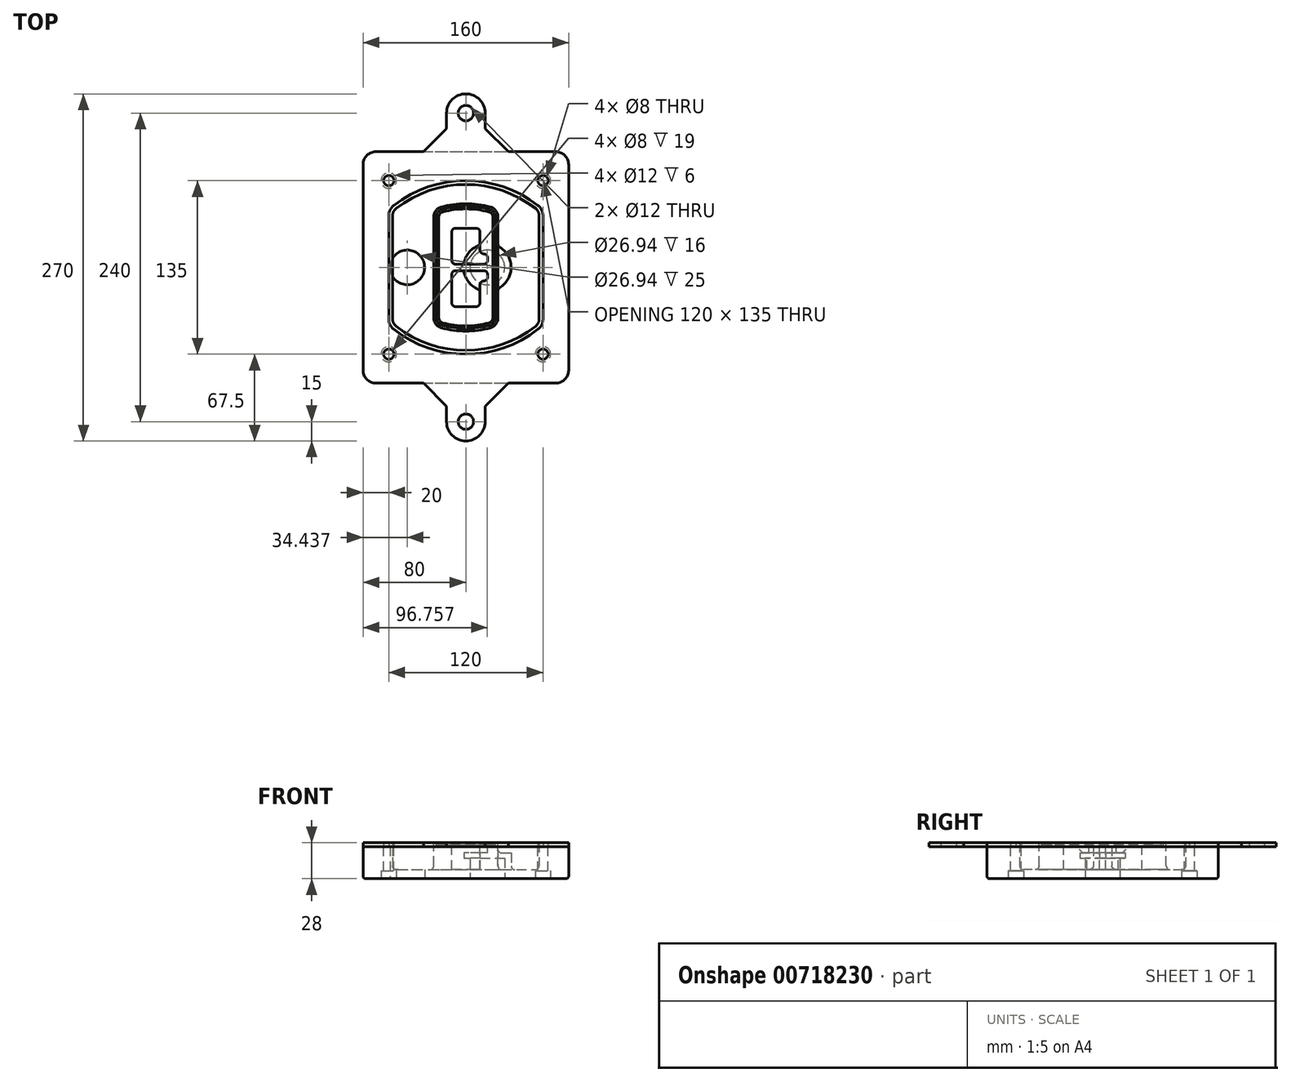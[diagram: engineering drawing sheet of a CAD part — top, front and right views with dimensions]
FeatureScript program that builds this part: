
annotation { "Feature Type Name" : "Feature", "Feature Type Description" : "" }
export const myFeature = defineFeature(function(context is Context, id is Id, definition is map)
    precondition{}
    {
        {
            var Q0;
            Q0=qCreatedBy(makeId("Top.planeOp"),FACE);
            var sketch = newSketch(context, id + "F0", { "sketchPlane" : qUnion([Q0])});
            skPoint(sketch, "E0.rect.middle", {"position": v(0, 0) * mm});
            skLineSegment(sketch, "E1.bottom", {"start": v(-70, -90) * mm, "end": v(70, -90) * mm});
            skLineSegment(sketch, "E1.top", {"start": v(-70, 90) * mm, "end": v(70, 90) * mm});
            skLineSegment(sketch, "E1.left", {"start": v(-80, -80) * mm, "end": v(-80, 80) * mm});
            skLineSegment(sketch, "E1.right", {"start": v(80, -80) * mm, "end": v(80, 80) * mm});
            skLineSegment(sketch, "E2", {"start": v(-80, 90) * mm, "end": v(80, -90) * mm, "construction": true});
            skLineSegment(sketch, "E3", {"start": v(80, 90) * mm, "end": v(-80, -90) * mm, "construction": true});
            skCircle(sketch, "E4", {"center": v(-60, 67.5) * mm, "radius": 4 * mm});
            skCircle(sketch, "E5", {"center": v(60, 67.5) * mm, "radius": 4 * mm});
            skCircle(sketch, "E6", {"center": v(60, -67.5) * mm, "radius": 4 * mm});
            skCircle(sketch, "E7", {"center": v(-60, -67.5) * mm, "radius": 4 * mm});
            skLineSegment(sketch, "E8", {"start": v(-60, 67.5) * mm, "end": v(60, 67.5) * mm, "construction": true});
            skLineSegment(sketch, "E9", {"start": v(60, 67.5) * mm, "end": v(60, -67.5) * mm, "construction": true});
            skLineSegment(sketch, "E10", {"start": v(60, -67.5) * mm, "end": v(-60, -67.5) * mm, "construction": true});
            skLineSegment(sketch, "E11", {"start": v(-60, -67.5) * mm, "end": v(-60, 67.5) * mm, "construction": true});
            skLineSegment(sketch, "E12", {"start": v(-60, 40.3) * mm, "end": v(-60, -40.3) * mm});
            skLineSegment(sketch, "E13", {"start": v(60, 40.3) * mm, "end": v(60, -40.3) * mm});
            skArc(sketch, "E14", {"start": v(56.15, 48.18) * mm, "mid": v(0, 67.5) * mm, "end": v(-56.15, 48.18) * mm});
            skArc(sketch, "E15", {"start": v(-56.15, -48.18) * mm, "mid": v(0, -67.5) * mm, "end": v(56.15, -48.18) * mm});
            skLineSegment(sketch, "E16", {"start": v(-60, 0) * mm, "end": v(60, 0) * mm, "construction": true});
            skPoint(sketch, "E17.visualSharp", {"position": v(-60, -45) * mm});
            skArc(sketch, "E17.filletArc", {"start": v(-60, -40.3) * mm, "mid": v(-58.99, -44.68) * mm, "end": v(-56.15, -48.18) * mm});
            skPoint(sketch, "E18.visualSharp", {"position": v(-60, 45) * mm});
            skArc(sketch, "E18.filletArc", {"start": v(-56.15, 48.18) * mm, "mid": v(-58.99, 44.68) * mm, "end": v(-60, 40.3) * mm});
            skPoint(sketch, "E19.visualSharp", {"position": v(60, 45) * mm});
            skArc(sketch, "E19.filletArc", {"start": v(60, 40.3) * mm, "mid": v(58.99, 44.68) * mm, "end": v(56.15, 48.18) * mm});
            skPoint(sketch, "E20.visualSharp", {"position": v(60, -45) * mm});
            skArc(sketch, "E20.filletArc", {"start": v(56.15, -48.18) * mm, "mid": v(58.99, -44.68) * mm, "end": v(60, -40.3) * mm});
            skPoint(sketch, "E21.visualSharp", {"position": v(-80, 90) * mm});
            skArc(sketch, "E21.filletArc", {"start": v(-70, 90) * mm, "mid": v(-77.07, 87.07) * mm, "end": v(-80, 80) * mm});
            skPoint(sketch, "E22.visualSharp", {"position": v(80, 90) * mm});
            skArc(sketch, "E22.filletArc", {"start": v(80, 80) * mm, "mid": v(77.07, 87.07) * mm, "end": v(70, 90) * mm});
            skPoint(sketch, "E23.visualSharp", {"position": v(80, -90) * mm});
            skArc(sketch, "E23.filletArc", {"start": v(70, -90) * mm, "mid": v(77.07, -87.07) * mm, "end": v(80, -80) * mm});
            skPoint(sketch, "E24.visualSharp", {"position": v(-80, -90) * mm});
            skArc(sketch, "E24.filletArc", {"start": v(-80, -80) * mm, "mid": v(-77.07, -87.07) * mm, "end": v(-70, -90) * mm});
            skArc(sketch, "E25.0", {"start": v(57, 40.3) * mm, "mid": v(56.3, 43.36) * mm, "end": v(54.3, 45.81) * mm});
            skLineSegment(sketch, "E25.1", {"start": v(57, 40.3) * mm, "end": v(57, -40.3) * mm});
            skArc(sketch, "E25.2", {"start": v(54.3, -45.81) * mm, "mid": v(56.3, -43.36) * mm, "end": v(57, -40.3) * mm});
            skArc(sketch, "E25.3", {"start": v(-54.3, -45.81) * mm, "mid": v(0, -64.5) * mm, "end": v(54.3, -45.81) * mm});
            skArc(sketch, "E25.4", {"start": v(-57, -40.3) * mm, "mid": v(-56.3, -43.36) * mm, "end": v(-54.3, -45.81) * mm});
            skArc(sketch, "E25.5", {"start": v(54.3, 45.81) * mm, "mid": v(0, 64.5) * mm, "end": v(-54.3, 45.81) * mm});
            skLineSegment(sketch, "E25.6", {"start": v(-57, 40.3) * mm, "end": v(-57, -40.3) * mm});
            skArc(sketch, "E25.7", {"start": v(-54.3, 45.81) * mm, "mid": v(-56.3, 43.36) * mm, "end": v(-57, 40.3) * mm});
            skArc(sketch, "E26.0", {"start": v(-58.62, 51.33) * mm, "mid": v(-62.58, 46.43) * mm, "end": v(-64, 40.3) * mm});
            skArc(sketch, "E26.1", {"start": v(58.62, 51.33) * mm, "mid": v(0, 71.5) * mm, "end": v(-58.62, 51.33) * mm});
            skArc(sketch, "E26.2", {"start": v(64, 40.3) * mm, "mid": v(62.58, 46.43) * mm, "end": v(58.62, 51.33) * mm});
            skLineSegment(sketch, "E26.3", {"start": v(64, 40.3) * mm, "end": v(64, -40.3) * mm});
            skArc(sketch, "E26.4", {"start": v(58.62, -51.33) * mm, "mid": v(62.58, -46.43) * mm, "end": v(64, -40.3) * mm});
            skLineSegment(sketch, "E26.5", {"start": v(-64, 40.3) * mm, "end": v(-64, -40.3) * mm});
            skArc(sketch, "E26.6", {"start": v(-58.62, -51.33) * mm, "mid": v(0, -71.5) * mm, "end": v(58.62, -51.33) * mm});
            skArc(sketch, "E26.7", {"start": v(-64, -40.3) * mm, "mid": v(-62.58, -46.43) * mm, "end": v(-58.62, -51.33) * mm});
            skSolve(sketch);
        }
        {
            var Q0;
            Q0=makeQuery(id+"F0.imprint","IMPRINT",FACE,{"disambiguationData":[TD([[makeQuery(id+"F0.imprint","IMPRINT",EDGE,{"derivedFrom":sQuery(id+"F0.wireOp",EDGE,"E1.bottom")}),1.0]])]});
            var Q1;
            Q1=makeQuery(id+"F0.imprint","IMPRINT",FACE,{"disambiguationData":[TD([[makeQuery(id+"F0.imprint","IMPRINT",EDGE,{"derivedFrom":sQuery(id+"F0.wireOp",EDGE,"E12")}),1.0]])]});
            var Q2;
            Q2=makeQuery(id+"F0.imprint","IMPRINT",FACE,{"disambiguationData":[TD([[makeQuery(id+"F0.imprint","IMPRINT",EDGE,{"derivedFrom":sQuery(id+"F0.wireOp",EDGE,"E25.0")}),1.0]])]});
            var Q3;
            Q3=makeQuery(id+"F0.imprint","IMPRINT",FACE,{"disambiguationData":[TD([[makeQuery(id+"F0.imprint","IMPRINT",EDGE,{"derivedFrom":sQuery(id+"F0.wireOp",EDGE,"E12")}),-1.0]])]});
            extrude(context, id + "F1", {"entities" : qUnion([Q0, Q1, Q2, Q3]), "oppositeDirection" : true, "depth" : 25 * mm});
        }
        {
            var Q0;
            Q0=makeQuery(id+"F0.imprint","IMPRINT",FACE,{"disambiguationData":[TD([[makeQuery(id+"F0.imprint","IMPRINT",EDGE,{"derivedFrom":sQuery(id+"F0.wireOp",EDGE,"E12")}),1.0]])]});
            extrude(context, id + "F2", {"entities" : qUnion([Q0]), "operationType" : NewBodyOperationType.ADD, "depth" : 3 * mm});
        }
        {
            var Q0;
            Q0=makeQuery(id+"F0.imprint","IMPRINT",FACE,{"disambiguationData":[TD([[makeQuery(id+"F0.imprint","IMPRINT",EDGE,{"derivedFrom":sQuery(id+"F0.wireOp",EDGE,"E25.0")}),1.0]])]});
            extrude(context, id + "F3", {"entities" : qUnion([Q0]), "operationType" : NewBodyOperationType.REMOVE, "oppositeDirection" : true, "depth" : 18 * mm});
        }
        {
            var Q0;
            Q0=makeQuery(id+"F2.opExtrude","CAP_FACE",FACE,{"disambiguationData":[OSD([sQuery(id+"F0.wireOp",EDGE,"E12"),sQuery(id+"F0.wireOp",EDGE,"E13"),sQuery(id+"F0.wireOp",EDGE,"E14"),sQuery(id+"F0.wireOp",EDGE,"E15"),sQuery(id+"F0.wireOp",EDGE,"E17.filletArc"),sQuery(id+"F0.wireOp",EDGE,"E18.filletArc"),sQuery(id+"F0.wireOp",EDGE,"E19.filletArc"),sQuery(id+"F0.wireOp",EDGE,"E20.filletArc"),sQuery(id+"F0.wireOp",EDGE,"E25.0"),sQuery(id+"F0.wireOp",EDGE,"E25.1"),sQuery(id+"F0.wireOp",EDGE,"E25.2"),sQuery(id+"F0.wireOp",EDGE,"E25.3"),sQuery(id+"F0.wireOp",EDGE,"E25.4"),sQuery(id+"F0.wireOp",EDGE,"E25.5"),sQuery(id+"F0.wireOp",EDGE,"E25.6"),sQuery(id+"F0.wireOp",EDGE,"E25.7")])],"isStart":false});
            var sketch = newSketch(context, id + "F4", { "sketchPlane" : qUnion([Q0])});
            skArc(sketch, "E27.0", {"start": v(-19.08, -46.97) * mm, "mid": v(0, -49.5) * mm, "end": v(19.08, -46.97) * mm});
            skArc(sketch, "E28.0", {"start": v(19.08, 46.97) * mm, "mid": v(0, 49.5) * mm, "end": v(-19.08, 46.97) * mm});
            skLineSegment(sketch, "E29", {"start": v(-25, 39.25) * mm, "end": v(-25, -39.25) * mm});
            skLineSegment(sketch, "E30", {"start": v(25, 39.25) * mm, "end": v(25, -39.25) * mm});
            skLineSegment(sketch, "E31", {"start": v(-25, 45.1) * mm, "end": v(25, 45.1) * mm, "construction": true});
            skLineSegment(sketch, "E32", {"start": v(-25, -45.1) * mm, "end": v(25, -45.1) * mm, "construction": true});
            skPoint(sketch, "E33.visualSharp", {"position": v(-25, 45.1) * mm});
            skArc(sketch, "E33.filletArc", {"start": v(-19.08, 46.97) * mm, "mid": v(-23.35, 44.11) * mm, "end": v(-25, 39.25) * mm});
            skPoint(sketch, "E34.visualSharp", {"position": v(25, 45.1) * mm});
            skArc(sketch, "E34.filletArc", {"start": v(25, 39.25) * mm, "mid": v(23.35, 44.11) * mm, "end": v(19.08, 46.97) * mm});
            skPoint(sketch, "E35.visualSharp", {"position": v(25, -45.1) * mm});
            skArc(sketch, "E35.filletArc", {"start": v(19.08, -46.97) * mm, "mid": v(23.35, -44.11) * mm, "end": v(25, -39.25) * mm});
            skPoint(sketch, "E36.visualSharp", {"position": v(-25, -45.1) * mm});
            skArc(sketch, "E36.filletArc", {"start": v(-25, -39.25) * mm, "mid": v(-23.35, -44.11) * mm, "end": v(-19.08, -46.97) * mm});
            skArc(sketch, "E37.0", {"start": v(54.3, 45.81) * mm, "mid": v(0, 64.5) * mm, "end": v(-54.3, 45.81) * mm});
            skArc(sketch, "E37.1", {"start": v(-54.3, 45.81) * mm, "mid": v(-56.3, 43.36) * mm, "end": v(-57, 40.3) * mm});
            skLineSegment(sketch, "E37.2", {"start": v(-57, 40.3) * mm, "end": v(-57, -40.3) * mm});
            skArc(sketch, "E37.3", {"start": v(-57, -40.3) * mm, "mid": v(-56.3, -43.36) * mm, "end": v(-54.3, -45.81) * mm});
            skArc(sketch, "E37.4", {"start": v(-54.3, -45.81) * mm, "mid": v(0, -64.5) * mm, "end": v(54.3, -45.81) * mm});
            skArc(sketch, "E37.5", {"start": v(54.3, -45.81) * mm, "mid": v(56.3, -43.36) * mm, "end": v(57, -40.3) * mm});
            skLineSegment(sketch, "E37.6", {"start": v(57, 40.3) * mm, "end": v(57, -40.3) * mm});
            skArc(sketch, "E37.7", {"start": v(57, 40.3) * mm, "mid": v(56.3, 43.36) * mm, "end": v(54.3, 45.81) * mm});
            skLineSegment(sketch, "E38.0", {"start": v(23, 39.25) * mm, "end": v(23, -39.25) * mm});
            skArc(sketch, "E38.1", {"start": v(18.56, -45.04) * mm, "mid": v(21.76, -42.9) * mm, "end": v(23, -39.25) * mm});
            skArc(sketch, "E38.2", {"start": v(-18.56, -45.04) * mm, "mid": v(0, -47.5) * mm, "end": v(18.56, -45.04) * mm});
            skArc(sketch, "E38.3", {"start": v(-23, -39.25) * mm, "mid": v(-21.76, -42.9) * mm, "end": v(-18.56, -45.04) * mm});
            skLineSegment(sketch, "E38.4", {"start": v(-23, 39.25) * mm, "end": v(-23, -39.25) * mm});
            skArc(sketch, "E38.5", {"start": v(23, 39.25) * mm, "mid": v(21.76, 42.9) * mm, "end": v(18.56, 45.04) * mm});
            skArc(sketch, "E38.6", {"start": v(-18.56, 45.04) * mm, "mid": v(-21.76, 42.9) * mm, "end": v(-23, 39.25) * mm});
            skArc(sketch, "E38.7", {"start": v(18.56, 45.04) * mm, "mid": v(0, 47.5) * mm, "end": v(-18.56, 45.04) * mm});
            skArc(sketch, "E39.0", {"start": v(21, 39.25) * mm, "mid": v(20.18, 41.68) * mm, "end": v(18.04, 43.1) * mm});
            skLineSegment(sketch, "E39.1", {"start": v(21, 39.25) * mm, "end": v(21, -39.25) * mm});
            skArc(sketch, "E39.2", {"start": v(18.04, -43.1) * mm, "mid": v(20.18, -41.68) * mm, "end": v(21, -39.25) * mm});
            skArc(sketch, "E39.3", {"start": v(-18.04, -43.1) * mm, "mid": v(0, -45.5) * mm, "end": v(18.04, -43.1) * mm});
            skArc(sketch, "E39.4", {"start": v(-21, -39.25) * mm, "mid": v(-20.18, -41.68) * mm, "end": v(-18.04, -43.1) * mm});
            skArc(sketch, "E39.5", {"start": v(18.04, 43.1) * mm, "mid": v(0, 45.5) * mm, "end": v(-18.04, 43.1) * mm});
            skLineSegment(sketch, "E39.6", {"start": v(-21, 39.25) * mm, "end": v(-21, -39.25) * mm});
            skArc(sketch, "E39.7", {"start": v(-18.04, 43.1) * mm, "mid": v(-20.18, 41.68) * mm, "end": v(-21, 39.25) * mm});
            skLineSegment(sketch, "E40", {"start": v(-25, 0) * mm, "end": v(25, 0) * mm, "construction": true});
            skLineSegment(sketch, "E41", {"start": v(-11, 5.5) * mm, "end": v(-11, 27.5) * mm});
            skLineSegment(sketch, "E42", {"start": v(-8, 30.5) * mm, "end": v(8, 30.5) * mm});
            skLineSegment(sketch, "E43", {"start": v(11, 27.5) * mm, "end": v(11, 13.5) * mm});
            skLineSegment(sketch, "E44", {"start": v(14, 10.5) * mm, "end": v(14, 10.5) * mm});
            skLineSegment(sketch, "E45", {"start": v(17, 7.5) * mm, "end": v(17, 5.5) * mm});
            skLineSegment(sketch, "E46", {"start": v(14, 2.5) * mm, "end": v(-8, 2.5) * mm});
            skPoint(sketch, "E47.visualSharp", {"position": v(-11, 30.5) * mm});
            skArc(sketch, "E47.filletArc", {"start": v(-8, 30.5) * mm, "mid": v(-10.12, 29.62) * mm, "end": v(-11, 27.5) * mm});
            skPoint(sketch, "E48.visualSharp", {"position": v(11, 30.5) * mm});
            skArc(sketch, "E48.filletArc", {"start": v(11, 27.5) * mm, "mid": v(10.12, 29.62) * mm, "end": v(8, 30.5) * mm});
            skPoint(sketch, "E49.visualSharp", {"position": v(11, 10.5) * mm});
            skArc(sketch, "E49.filletArc", {"start": v(11, 13.5) * mm, "mid": v(11.88, 11.38) * mm, "end": v(14, 10.5) * mm});
            skPoint(sketch, "E50.visualSharp", {"position": v(17, 10.5) * mm});
            skArc(sketch, "E50.filletArc", {"start": v(17, 7.5) * mm, "mid": v(16.12, 9.62) * mm, "end": v(14, 10.5) * mm});
            skPoint(sketch, "E51.visualSharp", {"position": v(17, 2.5) * mm});
            skArc(sketch, "E51.filletArc", {"start": v(14, 2.5) * mm, "mid": v(16.12, 3.38) * mm, "end": v(17, 5.5) * mm});
            skPoint(sketch, "E52.visualSharp", {"position": v(-11, 2.5) * mm});
            skArc(sketch, "E52.filletArc", {"start": v(-11, 5.5) * mm, "mid": v(-10.12, 3.38) * mm, "end": v(-8, 2.5) * mm});
            skLineSegment(sketch, "E53.0.MirrorCS", {"start": v(14, -2.5) * mm, "end": v(-8, -2.5) * mm});
            skArc(sketch, "E54.0.MirrorCS", {"start": v(-11, -5.5) * mm, "mid": v(-10.12, -3.38) * mm, "end": v(-8, -2.5) * mm});
            skLineSegment(sketch, "E55.0.MirrorCS", {"start": v(-11, -5.5) * mm, "end": v(-11, -27.5) * mm});
            skArc(sketch, "E56.0.MirrorCS", {"start": v(-8, -30.5) * mm, "mid": v(-10.12, -29.62) * mm, "end": v(-11, -27.5) * mm});
            skLineSegment(sketch, "E57.0.MirrorCS", {"start": v(-8, -30.5) * mm, "end": v(8, -30.5) * mm});
            skArc(sketch, "E58.0.MirrorCS", {"start": v(11, -27.5) * mm, "mid": v(10.12, -29.62) * mm, "end": v(8, -30.5) * mm});
            skLineSegment(sketch, "E59.0.MirrorCS", {"start": v(11, -27.5) * mm, "end": v(11, -13.5) * mm});
            skArc(sketch, "E60.0.MirrorCS", {"start": v(11, -13.5) * mm, "mid": v(11.88, -11.38) * mm, "end": v(14, -10.5) * mm});
            skArc(sketch, "E61.0.MirrorCS", {"start": v(17, -7.5) * mm, "mid": v(16.12, -9.62) * mm, "end": v(14, -10.5) * mm});
            skLineSegment(sketch, "E62.0.MirrorCS", {"start": v(17, -7.5) * mm, "end": v(17, -5.5) * mm});
            skArc(sketch, "E63.0.MirrorCS", {"start": v(14, -2.5) * mm, "mid": v(16.12, -3.38) * mm, "end": v(17, -5.5) * mm});
            skSolve(sketch);
        }
        {
            var Q0;
            Q0=makeQuery(id+"F4.imprint","IMPRINT",FACE,{"disambiguationData":[TD([[makeQuery(id+"F4.imprint","IMPRINT",EDGE,{"derivedFrom":sQuery(id+"F4.wireOp",EDGE,"E27.0")}),1.0]])]});
            var Q1;
            Q1=makeQuery(id+"F4.imprint","IMPRINT",FACE,{"disambiguationData":[TD([[makeQuery(id+"F4.imprint","IMPRINT",EDGE,{"derivedFrom":sQuery(id+"F4.wireOp",EDGE,"E38.0")}),-1.0]])]});
            var Q2;
            Q2=makeQuery(id+"F4.imprint","IMPRINT",FACE,{"disambiguationData":[TD([[makeQuery(id+"F4.imprint","IMPRINT",EDGE,{"derivedFrom":sQuery(id+"F4.wireOp",EDGE,"E39.0")}),1.0]])]});
            extrude(context, id + "F5", {"entities" : qUnion([Q0, Q1, Q2]), "operationType" : NewBodyOperationType.ADD, "endBound" : BoundingType.UP_TO_NEXT, "oppositeDirection" : true, "depth" : 25 * mm});
        }
        {
            var Q0;
            Q0=makeQuery(id+"F4.imprint","IMPRINT",FACE,{"disambiguationData":[TD([[makeQuery(id+"F4.imprint","IMPRINT",EDGE,{"derivedFrom":sQuery(id+"F4.wireOp",EDGE,"E38.0")}),-1.0]])]});
            extrude(context, id + "F6", {"entities" : qUnion([Q0]), "operationType" : NewBodyOperationType.REMOVE, "oppositeDirection" : true, "depth" : 2 * mm});
        }
        {
            var Q0;
            Q0=makeQuery(id+"F1.opExtrude","CAP_FACE",FACE,{"disambiguationData":[OSD([sQuery(id+"F0.wireOp",EDGE,"E1.bottom"),sQuery(id+"F0.wireOp",EDGE,"E1.top"),sQuery(id+"F0.wireOp",EDGE,"E1.left"),sQuery(id+"F0.wireOp",EDGE,"E1.right"),sQuery(id+"F0.wireOp",EDGE,"E4"),sQuery(id+"F0.wireOp",EDGE,"E5"),sQuery(id+"F0.wireOp",EDGE,"E6"),sQuery(id+"F0.wireOp",EDGE,"E7"),sQuery(id+"F0.wireOp",EDGE,"E21.filletArc"),sQuery(id+"F0.wireOp",EDGE,"E22.filletArc"),sQuery(id+"F0.wireOp",EDGE,"E23.filletArc"),sQuery(id+"F0.wireOp",EDGE,"E24.filletArc")])],"isStart":false});
            var sketch = newSketch(context, id + "F7", { "sketchPlane" : qUnion([Q0])});
            skCircle(sketch, "E64", {"center": v(16.76, 0) * mm, "radius": 13.47 * mm});
            skCircle(sketch, "E65", {"center": v(-45.56, 0) * mm, "radius": 13.47 * mm});
            skLineSegment(sketch, "E66", {"start": v(80, 0) * mm, "end": v(-80, 0) * mm});
            skCircle(sketch, "E67", {"center": v(16.76, 0) * mm, "radius": 18.47 * mm});
            skCircle(sketch, "E68", {"center": v(60, -67.5) * mm, "radius": 6 * mm});
            skCircle(sketch, "E69", {"center": v(-60, -67.5) * mm, "radius": 6 * mm});
            skCircle(sketch, "E70", {"center": v(-60, 67.5) * mm, "radius": 6 * mm});
            skCircle(sketch, "E71", {"center": v(60, 67.5) * mm, "radius": 6 * mm});
            skSolve(sketch);
        }
        {
            var Q0;
            {var subQ1=sQuery(id+"F7.wireOp",EDGE,"E66");var subQ4=sQuery(id+"F7.wireOp",EDGE,"E64");var subQ6=makeQuery(id+"F7.imprint","INTERSECT",VERTEX,{"disambiguationData":[OD(0.0)],"derivedFrom":[subQ4,subQ1]});Q0=makeQuery(id+"F7.imprint","IMPRINT",FACE,{"disambiguationData":[TD([[makeQuery(id+"F7.imprint","IMPRINT",EDGE,{"disambiguationData":[TD([[subQ6,-1.0]])],"derivedFrom":subQ4}),-1.0]])]});}
            var Q1;
            {var subQ0=sQuery(id+"F7.wireOp",EDGE,"E66");var subQ1=sQuery(id+"F7.wireOp",EDGE,"E64");var subQ3=makeQuery(id+"F7.imprint","INTERSECT",VERTEX,{"disambiguationData":[OD(0.0)],"derivedFrom":[subQ1,subQ0]});Q1=makeQuery(id+"F7.imprint","IMPRINT",FACE,{"disambiguationData":[TD([[makeQuery(id+"F7.imprint","IMPRINT",EDGE,{"disambiguationData":[TD([[subQ3,-1.0]])],"derivedFrom":subQ1}),1.0]])]});}
            var Q2;
            {var subQ0=sQuery(id+"F7.wireOp",EDGE,"E66");var subQ1=sQuery(id+"F7.wireOp",EDGE,"E64");var subQ3=makeQuery(id+"F7.imprint","INTERSECT",VERTEX,{"disambiguationData":[OD(0.0)],"derivedFrom":[subQ1,subQ0]});Q2=makeQuery(id+"F7.imprint","IMPRINT",FACE,{"disambiguationData":[TD([[makeQuery(id+"F7.imprint","IMPRINT",EDGE,{"disambiguationData":[TD([[subQ3,1.0]])],"derivedFrom":subQ1}),1.0]])]});}
            var Q3;
            {var subQ1=sQuery(id+"F7.wireOp",EDGE,"E66");var subQ4=sQuery(id+"F7.wireOp",EDGE,"E64");var subQ6=makeQuery(id+"F7.imprint","INTERSECT",VERTEX,{"disambiguationData":[OD(0.0)],"derivedFrom":[subQ4,subQ1]});Q3=makeQuery(id+"F7.imprint","IMPRINT",FACE,{"disambiguationData":[TD([[makeQuery(id+"F7.imprint","IMPRINT",EDGE,{"disambiguationData":[TD([[subQ6,1.0]])],"derivedFrom":subQ4}),-1.0]])]});}
            extrude(context, id + "F8", {"entities" : qUnion([Q0, Q1, Q2, Q3]), "operationType" : NewBodyOperationType.ADD, "oppositeDirection" : true, "depth" : 20 * mm});
        }
        {
            var Q0;
            {var subQ0=sQuery(id+"F7.wireOp",EDGE,"E66");var subQ1=sQuery(id+"F7.wireOp",EDGE,"E64");var subQ3=makeQuery(id+"F7.imprint","INTERSECT",VERTEX,{"disambiguationData":[OD(0.0)],"derivedFrom":[subQ1,subQ0]});Q0=makeQuery(id+"F7.imprint","IMPRINT",FACE,{"disambiguationData":[TD([[makeQuery(id+"F7.imprint","IMPRINT",EDGE,{"disambiguationData":[TD([[subQ3,-1.0]])],"derivedFrom":subQ1}),1.0]])]});}
            var Q1;
            {var subQ0=sQuery(id+"F7.wireOp",EDGE,"E66");var subQ1=sQuery(id+"F7.wireOp",EDGE,"E64");var subQ3=makeQuery(id+"F7.imprint","INTERSECT",VERTEX,{"disambiguationData":[OD(0.0)],"derivedFrom":[subQ1,subQ0]});Q1=makeQuery(id+"F7.imprint","IMPRINT",FACE,{"disambiguationData":[TD([[makeQuery(id+"F7.imprint","IMPRINT",EDGE,{"disambiguationData":[TD([[subQ3,1.0]])],"derivedFrom":subQ1}),1.0]])]});}
            extrude(context, id + "F9", {"entities" : qUnion([Q0, Q1]), "operationType" : NewBodyOperationType.REMOVE, "oppositeDirection" : true, "depth" : 16 * mm});
        }
        {
            var Q0;
            {var subQ0=sQuery(id+"F7.wireOp",EDGE,"E66");var subQ1=sQuery(id+"F7.wireOp",EDGE,"E65");var subQ3=makeQuery(id+"F7.imprint","INTERSECT",VERTEX,{"disambiguationData":[OD(0.0)],"derivedFrom":[subQ1,subQ0]});Q0=makeQuery(id+"F7.imprint","IMPRINT",FACE,{"disambiguationData":[TD([[makeQuery(id+"F7.imprint","IMPRINT",EDGE,{"disambiguationData":[TD([[subQ3,-1.0]])],"derivedFrom":subQ1}),1.0]])]});}
            var Q1;
            {var subQ0=sQuery(id+"F7.wireOp",EDGE,"E66");var subQ1=sQuery(id+"F7.wireOp",EDGE,"E65");var subQ3=makeQuery(id+"F7.imprint","INTERSECT",VERTEX,{"disambiguationData":[OD(0.0)],"derivedFrom":[subQ1,subQ0]});Q1=makeQuery(id+"F7.imprint","IMPRINT",FACE,{"disambiguationData":[TD([[makeQuery(id+"F7.imprint","IMPRINT",EDGE,{"disambiguationData":[TD([[subQ3,1.0]])],"derivedFrom":subQ1}),1.0]])]});}
            extrude(context, id + "F10", {"entities" : qUnion([Q0, Q1]), "operationType" : NewBodyOperationType.REMOVE, "oppositeDirection" : true, "depth" : 25 * mm});
        }
        {
            var Q0;
            Q0=makeQuery(id+"F7.imprint","IMPRINT",FACE,{"disambiguationData":[TD([[makeQuery(id+"F7.imprint","IMPRINT",EDGE,{"derivedFrom":sQuery(id+"F7.wireOp",EDGE,"E68")}),1.0]])]});
            var Q1;
            Q1=makeQuery(id+"F7.imprint","IMPRINT",FACE,{"disambiguationData":[TD([[makeQuery(id+"F7.imprint","IMPRINT",EDGE,{"derivedFrom":makeQuery(id+"F1.opExtrude","CAP_EDGE",EDGE,{"disambiguationData":[OSD([sQuery(id+"F0.wireOp",EDGE,"E5")])],"isStart":false})}),-1.0]])]});
            var Q2;
            Q2=makeQuery(id+"F7.imprint","IMPRINT",FACE,{"disambiguationData":[TD([[makeQuery(id+"F7.imprint","IMPRINT",EDGE,{"derivedFrom":sQuery(id+"F7.wireOp",EDGE,"E69")}),1.0]])]});
            var Q3;
            Q3=makeQuery(id+"F7.imprint","IMPRINT",FACE,{"disambiguationData":[TD([[makeQuery(id+"F7.imprint","IMPRINT",EDGE,{"derivedFrom":makeQuery(id+"F1.opExtrude","CAP_EDGE",EDGE,{"disambiguationData":[OSD([sQuery(id+"F0.wireOp",EDGE,"E4")])],"isStart":false})}),-1.0]])]});
            var Q4;
            Q4=makeQuery(id+"F7.imprint","IMPRINT",FACE,{"disambiguationData":[TD([[makeQuery(id+"F7.imprint","IMPRINT",EDGE,{"derivedFrom":sQuery(id+"F7.wireOp",EDGE,"E70")}),1.0]])]});
            var Q5;
            Q5=makeQuery(id+"F7.imprint","IMPRINT",FACE,{"disambiguationData":[TD([[makeQuery(id+"F7.imprint","IMPRINT",EDGE,{"derivedFrom":makeQuery(id+"F1.opExtrude","CAP_EDGE",EDGE,{"disambiguationData":[OSD([sQuery(id+"F0.wireOp",EDGE,"E7")])],"isStart":false})}),-1.0]])]});
            var Q6;
            Q6=makeQuery(id+"F7.imprint","IMPRINT",FACE,{"disambiguationData":[TD([[makeQuery(id+"F7.imprint","IMPRINT",EDGE,{"derivedFrom":sQuery(id+"F7.wireOp",EDGE,"E71")}),1.0]])]});
            var Q7;
            Q7=makeQuery(id+"F7.imprint","IMPRINT",FACE,{"disambiguationData":[TD([[makeQuery(id+"F7.imprint","IMPRINT",EDGE,{"derivedFrom":makeQuery(id+"F1.opExtrude","CAP_EDGE",EDGE,{"disambiguationData":[OSD([sQuery(id+"F0.wireOp",EDGE,"E6")])],"isStart":false})}),-1.0]])]});
            extrude(context, id + "F11", {"entities" : qUnion([Q0, Q1, Q2, Q3, Q4, Q5, Q6, Q7]), "operationType" : NewBodyOperationType.REMOVE, "oppositeDirection" : true, "depth" : 6 * mm});
        }
        {
            var Q0;
            Q0=makeQuery(id+"F9.boolean.opBoolean","COPY",FACE,{"derivedFrom":makeQuery(id+"F9.opExtrude","CAP_FACE",FACE,{"disambiguationData":[OSD([sQuery(id+"F7.wireOp",EDGE,"E64")])],"isStart":false})});
            var sketch = newSketch(context, id + "F12", { "sketchPlane" : qUnion([Q0])});
            skArc(sketch, "E72.0", {"start": v(11, 17.55) * mm, "mid": v(2.57, 11.82) * mm, "end": v(-1.54, 2.5) * mm});
            skArc(sketch, "E72.1", {"start": v(-1.54, -2.5) * mm, "mid": v(2.57, -11.82) * mm, "end": v(11, -17.55) * mm});
            skLineSegment(sketch, "E73", {"start": v(-1.54, -2.5) * mm, "end": v(14, -2.5) * mm});
            skLineSegment(sketch, "E74.0", {"start": v(14, 2.5) * mm, "end": v(-1.54, 2.5) * mm});
            skArc(sketch, "E74.1", {"start": v(14, 2.5) * mm, "mid": v(16.12, 3.38) * mm, "end": v(17, 5.5) * mm});
            skLineSegment(sketch, "E74.2", {"start": v(17, 7.5) * mm, "end": v(17, 5.5) * mm});
            skArc(sketch, "E74.3", {"start": v(17, 7.5) * mm, "mid": v(16.12, 9.62) * mm, "end": v(14, 10.5) * mm});
            skArc(sketch, "E74.4", {"start": v(11, 13.5) * mm, "mid": v(11.88, 11.38) * mm, "end": v(14, 10.5) * mm});
            skLineSegment(sketch, "E74.5", {"start": v(11, 17.55) * mm, "end": v(11, 13.5) * mm});
            skLineSegment(sketch, "E74.7", {"start": v(14, -2.5) * mm, "end": v(-1.54, -2.5) * mm});
            skArc(sketch, "E74.8", {"start": v(14, -2.5) * mm, "mid": v(16.12, -3.38) * mm, "end": v(17, -5.5) * mm});
            skLineSegment(sketch, "E74.9", {"start": v(17, -7.5) * mm, "end": v(17, -5.5) * mm});
            skArc(sketch, "E74.10", {"start": v(17, -7.5) * mm, "mid": v(16.12, -9.62) * mm, "end": v(14, -10.5) * mm});
            skArc(sketch, "E74.11", {"start": v(11, -13.5) * mm, "mid": v(11.88, -11.38) * mm, "end": v(14, -10.5) * mm});
            skLineSegment(sketch, "E74.12", {"start": v(11, -17.55) * mm, "end": v(11, -13.5) * mm});
            skPoint(sketch, "E75.orphan", {"position": v(11, -27.5) * mm});
            skPoint(sketch, "E76.orphan", {"position": v(-8, -2.5) * mm});
            skPoint(sketch, "E77.orphan", {"position": v(-8, 2.5) * mm});
            skPoint(sketch, "E78.orphan", {"position": v(11, 27.5) * mm});
            skSolve(sketch);
        }
        {
            var Q0;
            {var subQ7=sQuery(id+"F12.wireOp",EDGE,"E72.0");var subQ14=sQuery(id+"F12.wireOp",EDGE,"E72.1");var subQ16=sQuery(id+"F12.wireOp",EDGE,"E74.1");var subQ18=sQuery(id+"F12.wireOp",EDGE,"E74.8");Q0=qUnion([makeQuery(id+"F12.imprint","IMPRINT",FACE,{"disambiguationData":[TD([[makeQuery(id+"F12.imprint","IMPRINT",EDGE,{"derivedFrom":subQ7}),1.0]])]}),makeQuery(id+"F12.imprint","IMPRINT",FACE,{"disambiguationData":[TD([[makeQuery(id+"F12.imprint","IMPRINT",EDGE,{"derivedFrom":subQ14}),1.0]])]}),makeQuery(id+"F12.imprint","IMPRINT",FACE,{"disambiguationData":[TD([[makeQuery(id+"F12.imprint","IMPRINT",EDGE,{"derivedFrom":subQ16}),1.0]])]}),makeQuery(id+"F12.imprint","IMPRINT",FACE,{"disambiguationData":[TD([[makeQuery(id+"F12.imprint","IMPRINT",EDGE,{"derivedFrom":subQ18}),-1.0]])]})]);}
            var Q1;
            Q1=makeQuery(id+"F5.boolean.opBoolean","SPLIT",FACE,{"disambiguationData":[TD([makeQuery(id+"F5.opExtrude","SWEPT_FACE",FACE,{"disambiguationData":[OSD([sQuery(id+"F4.wireOp",EDGE,"E41")])]})])],"derivedFrom":makeQuery(id+"F3.boolean.opBoolean","COPY",FACE,{"derivedFrom":makeQuery(id+"F3.opExtrude","CAP_FACE",FACE,{"disambiguationData":[OSD([sQuery(id+"F0.wireOp",EDGE,"E25.0"),sQuery(id+"F0.wireOp",EDGE,"E25.1"),sQuery(id+"F0.wireOp",EDGE,"E25.2"),sQuery(id+"F0.wireOp",EDGE,"E25.3"),sQuery(id+"F0.wireOp",EDGE,"E25.4"),sQuery(id+"F0.wireOp",EDGE,"E25.5"),sQuery(id+"F0.wireOp",EDGE,"E25.6"),sQuery(id+"F0.wireOp",EDGE,"E25.7")])],"isStart":false})})});
            extrude(context, id + "F13", {"entities" : qUnion([Q0]), "operationType" : NewBodyOperationType.REMOVE, "endBound" : BoundingType.UP_TO_SURFACE, "endBoundEntityFace" : qUnion([Q1]), "depth" : 25 * mm});
        }
        {
            var Q0;
            Q0=makeQuery(id+"F3.boolean.opBoolean","COPY",EDGE,{"derivedFrom":makeQuery(id+"F3.opExtrude","CAP_EDGE",EDGE,{"disambiguationData":[OSD([sQuery(id+"F0.wireOp",EDGE,"E25.6")])],"isStart":false})});
            var Q1;
            Q1=makeQuery(id+"F8.boolean.opBoolean","INTERSECT",EDGE,{"derivedFrom":[makeQuery(id+"F5.opExtrude","SWEPT_FACE",FACE,{"disambiguationData":[OSD([sQuery(id+"F4.wireOp",EDGE,"E30")])]}),makeQuery(id+"F8.opExtrude","CAP_FACE",FACE,{"disambiguationData":[OSD([sQuery(id+"F7.wireOp",EDGE,"E67")])],"isStart":false})]});
            var Q2;
            Q2=makeQuery(id+"F8.boolean.opBoolean","INTERSECT",EDGE,{"disambiguationData":[OD(1.0)],"derivedFrom":[makeQuery(id+"F5.opExtrude","SWEPT_FACE",FACE,{"disambiguationData":[OSD([sQuery(id+"F4.wireOp",EDGE,"E30")])]}),makeQuery(id+"F8.opExtrude","SWEPT_FACE",FACE,{"disambiguationData":[OSD([sQuery(id+"F7.wireOp",EDGE,"E67")])]})]});
            var Q3;
            {var subQ0=sQuery(id+"F4.wireOp",EDGE,"E30");Q3=makeQuery(id+"F8.boolean.opBoolean","SPLIT",EDGE,{"disambiguationData":[TD([makeQuery(id+"F5.opExtrude","SWEPT_FACE",FACE,{"disambiguationData":[OSD([sQuery(id+"F4.wireOp",EDGE,"E35.filletArc")])]})])],"derivedFrom":makeQuery(id+"F5.opExtrude","CAP_EDGE",EDGE,{"disambiguationData":[OSD([subQ0])],"isStart":false})});}
            var Q4;
            {var subQ0=sQuery(id+"F0.wireOp",EDGE,"E25.7");var subQ1=sQuery(id+"F0.wireOp",EDGE,"E25.1");var subQ2=sQuery(id+"F0.wireOp",EDGE,"E25.6");var subQ3=sQuery(id+"F0.wireOp",EDGE,"E25.5");var subQ4=sQuery(id+"F0.wireOp",EDGE,"E25.4");var subQ5=sQuery(id+"F0.wireOp",EDGE,"E25.0");var subQ6=sQuery(id+"F0.wireOp",EDGE,"E25.2");var subQ7=sQuery(id+"F0.wireOp",EDGE,"E25.3");Q4=makeQuery(id+"F8.boolean.opBoolean","INTERSECT",EDGE,{"derivedFrom":[makeQuery(id+"F5.boolean.opBoolean","SPLIT",FACE,{"disambiguationData":[TD([makeQuery(id+"F2.opExtrude","SWEPT_FACE",FACE,{"disambiguationData":[OSD([subQ5])]})])],"derivedFrom":makeQuery(id+"F3.boolean.opBoolean","COPY",FACE,{"derivedFrom":makeQuery(id+"F3.opExtrude","CAP_FACE",FACE,{"disambiguationData":[OSD([subQ5,subQ1,subQ6,subQ7,subQ4,subQ3,subQ2,subQ0])],"isStart":false})})}),makeQuery(id+"F8.opExtrude","SWEPT_FACE",FACE,{"disambiguationData":[OSD([sQuery(id+"F7.wireOp",EDGE,"E67")])]})]});}
            var Q5;
            Q5=makeQuery(id+"F8.boolean.opBoolean","INTERSECT",EDGE,{"disambiguationData":[OD(0.0)],"derivedFrom":[makeQuery(id+"F5.opExtrude","SWEPT_FACE",FACE,{"disambiguationData":[OSD([sQuery(id+"F4.wireOp",EDGE,"E30")])]}),makeQuery(id+"F8.opExtrude","SWEPT_FACE",FACE,{"disambiguationData":[OSD([sQuery(id+"F7.wireOp",EDGE,"E67")])]})]});
            fillet(context, id + "F14", {"entities" : qUnion([Q0, Q1, Q2, Q3, Q4, Q5]), "radius" : 3 * mm, "tangentPropagation" : true, "allowEdgeOverflow" : false});
        }
        {
            var Q0;
            Q0=makeQuery(id+"F1.opExtrude","CAP_EDGE",EDGE,{"disambiguationData":[OSD([sQuery(id+"F0.wireOp",EDGE,"E1.bottom")])],"isStart":false});
            fillet(context, id + "F15", {"entities" : qUnion([Q0]), "radius" : 2 * mm, "tangentPropagation" : true, "allowEdgeOverflow" : false});
        }
        {
            var Q0;
            {var subQ0=sQuery(id+"F0.wireOp",EDGE,"E21.filletArc");var subQ1=sQuery(id+"F0.wireOp",EDGE,"E7");var subQ2=sQuery(id+"F0.wireOp",EDGE,"E6");var subQ3=sQuery(id+"F0.wireOp",EDGE,"E5");var subQ4=sQuery(id+"F0.wireOp",EDGE,"E4");var subQ5=sQuery(id+"F0.wireOp",EDGE,"E22.filletArc");var subQ6=sQuery(id+"F0.wireOp",EDGE,"E1.bottom");var subQ7=sQuery(id+"F0.wireOp",EDGE,"E1.right");var subQ8=sQuery(id+"F0.wireOp",EDGE,"E1.top");var subQ9=sQuery(id+"F0.wireOp",EDGE,"E1.left");var subQ10=sQuery(id+"F0.wireOp",EDGE,"E23.filletArc");var subQ11=sQuery(id+"F0.wireOp",EDGE,"E24.filletArc");Q0=makeQuery(id+"F2.boolean.opBoolean","SPLIT",FACE,{"disambiguationData":[TD([makeQuery(id+"F1.opExtrude","SWEPT_FACE",FACE,{"disambiguationData":[OSD([subQ6])]})])],"derivedFrom":makeQuery(id+"F1.opExtrude","CAP_FACE",FACE,{"disambiguationData":[OSD([subQ6,subQ8,subQ9,subQ7,subQ4,subQ3,subQ2,subQ1,subQ0,subQ5,subQ10,subQ11])],"isStart":true})});}
            var sketch = newSketch(context, id + "F16", { "sketchPlane" : qUnion([Q0])});
            skLineSegment(sketch, "E79.0", {"start": v(-70, 90) * mm, "end": v(70, 90) * mm});
            skArc(sketch, "E79.1", {"start": v(-70, 90) * mm, "mid": v(-77.07, 87.07) * mm, "end": v(-80, 80) * mm});
            skLineSegment(sketch, "E79.2", {"start": v(-80, -80) * mm, "end": v(-80, 80) * mm});
            skArc(sketch, "E79.3", {"start": v(80, 80) * mm, "mid": v(77.07, 87.07) * mm, "end": v(70, 90) * mm});
            skLineSegment(sketch, "E79.4", {"start": v(80, -80) * mm, "end": v(80, 80) * mm});
            skArc(sketch, "E79.5", {"start": v(70, -90) * mm, "mid": v(77.07, -87.07) * mm, "end": v(80, -80) * mm});
            skLineSegment(sketch, "E79.6", {"start": v(-70, -90) * mm, "end": v(70, -90) * mm});
            skArc(sketch, "E79.7", {"start": v(-80, -80) * mm, "mid": v(-77.07, -87.07) * mm, "end": v(-70, -90) * mm});
            skCircle(sketch, "E79.8", {"center": v(-60, -67.5) * mm, "radius": 4 * mm});
            skCircle(sketch, "E79.9", {"center": v(-60, 67.5) * mm, "radius": 4 * mm});
            skCircle(sketch, "E79.10", {"center": v(60, 67.5) * mm, "radius": 4 * mm});
            skCircle(sketch, "E79.11", {"center": v(60, -67.5) * mm, "radius": 4 * mm});
            skArc(sketch, "E79.12", {"start": v(-56.15, -48.18) * mm, "mid": v(0, -67.5) * mm, "end": v(56.15, -48.18) * mm});
            skLineSegment(sketch, "E79.13", {"start": v(60, 40.3) * mm, "end": v(60, -40.3) * mm});
            skArc(sketch, "E79.14", {"start": v(56.15, -48.18) * mm, "mid": v(58.99, -44.68) * mm, "end": v(60, -40.3) * mm});
            skArc(sketch, "E79.15", {"start": v(56.15, 48.18) * mm, "mid": v(0, 67.5) * mm, "end": v(-56.15, 48.18) * mm});
            skArc(sketch, "E79.16", {"start": v(-56.15, 48.18) * mm, "mid": v(-58.99, 44.68) * mm, "end": v(-60, 40.3) * mm});
            skLineSegment(sketch, "E79.17", {"start": v(-60, 40.3) * mm, "end": v(-60, -40.3) * mm});
            skArc(sketch, "E79.18", {"start": v(60, 40.3) * mm, "mid": v(58.99, 44.68) * mm, "end": v(56.15, 48.18) * mm});
            skArc(sketch, "E79.19", {"start": v(-60, -40.3) * mm, "mid": v(-58.99, -44.68) * mm, "end": v(-56.15, -48.18) * mm});
            skLineSegment(sketch, "E80", {"start": v(0, -90) * mm, "end": v(0, -120) * mm, "construction": true});
            skLineSegment(sketch, "E81", {"start": v(-15, -108) * mm, "end": v(-15, -120) * mm});
            skLineSegment(sketch, "E82", {"start": v(-33, -90) * mm, "end": v(-15, -108) * mm});
            skArc(sketch, "E83", {"start": v(-15, -120) * mm, "mid": v(0, -135) * mm, "end": v(15, -120) * mm});
            skLineSegment(sketch, "E84", {"start": v(15, -120) * mm, "end": v(15, -108) * mm});
            skLineSegment(sketch, "E85", {"start": v(15, -108) * mm, "end": v(33, -90) * mm});
            skCircle(sketch, "E86", {"center": v(0, -120) * mm, "radius": 6 * mm});
            skLineSegment(sketch, "E87", {"start": v(80, 0) * mm, "end": v(-80, 0) * mm, "construction": true});
            skLineSegment(sketch, "E88.MirrorCS", {"start": v(-33, 90) * mm, "end": v(-15, 108) * mm});
            skLineSegment(sketch, "E89.MirrorCS", {"start": v(-15, 108) * mm, "end": v(-15, 120) * mm});
            skArc(sketch, "E90.MirrorCS", {"start": v(-15, 120) * mm, "mid": v(0, 135) * mm, "end": v(15, 120) * mm});
            skLineSegment(sketch, "E91.MirrorCS", {"start": v(15, 120) * mm, "end": v(15, 108) * mm});
            skLineSegment(sketch, "E92.MirrorCS", {"start": v(15, 108) * mm, "end": v(33, 90) * mm});
            skCircle(sketch, "E93.MirrorC", {"center": v(0, 120) * mm, "radius": 6 * mm});
            skLineSegment(sketch, "E94.MirrorCS", {"start": v(0, 90) * mm, "end": v(0, 120) * mm, "construction": true});
            skSolve(sketch);
        }
        {
            var Q0;
            {var subQ4=sQuery(id+"F16.wireOp",EDGE,"E79.1");Q0=makeQuery(id+"F16.imprint","IMPRINT",FACE,{"disambiguationData":[TD([[makeQuery(id+"F16.imprint","IMPRINT",EDGE,{"derivedFrom":subQ4}),1.0]])]});}
            var Q1;
            {var subQ0=sQuery(id+"F16.wireOp",EDGE,"E88.MirrorCS");Q1=makeQuery(id+"F16.imprint","IMPRINT",FACE,{"disambiguationData":[TD([[makeQuery(id+"F16.imprint","IMPRINT",EDGE,{"derivedFrom":subQ0}),-1.0]])]});}
            var Q2;
            Q2=makeQuery(id+"F16.imprint","IMPRINT",FACE,{"disambiguationData":[TD([[makeQuery(id+"F16.imprint","IMPRINT",EDGE,{"derivedFrom":sQuery(id+"F16.wireOp",EDGE,"E81")}),1.0]])]});
            var Q3;
            Q3=makeQuery(id+"F2.opExtrude","CAP_FACE",FACE,{"disambiguationData":[OSD([sQuery(id+"F0.wireOp",EDGE,"E12"),sQuery(id+"F0.wireOp",EDGE,"E13"),sQuery(id+"F0.wireOp",EDGE,"E14"),sQuery(id+"F0.wireOp",EDGE,"E15"),sQuery(id+"F0.wireOp",EDGE,"E17.filletArc"),sQuery(id+"F0.wireOp",EDGE,"E18.filletArc"),sQuery(id+"F0.wireOp",EDGE,"E19.filletArc"),sQuery(id+"F0.wireOp",EDGE,"E20.filletArc"),sQuery(id+"F0.wireOp",EDGE,"E25.0"),sQuery(id+"F0.wireOp",EDGE,"E25.1"),sQuery(id+"F0.wireOp",EDGE,"E25.2"),sQuery(id+"F0.wireOp",EDGE,"E25.3"),sQuery(id+"F0.wireOp",EDGE,"E25.4"),sQuery(id+"F0.wireOp",EDGE,"E25.5"),sQuery(id+"F0.wireOp",EDGE,"E25.6"),sQuery(id+"F0.wireOp",EDGE,"E25.7")])],"isStart":false});
            extrude(context, id + "F17", {"entities" : qUnion([Q0, Q1, Q2]), "endBound" : BoundingType.UP_TO_SURFACE, "depth" : 5 * mm, "endBoundEntityFace" : qUnion([Q3]), "offsetDistance" : 25 * mm});
        }
    });
